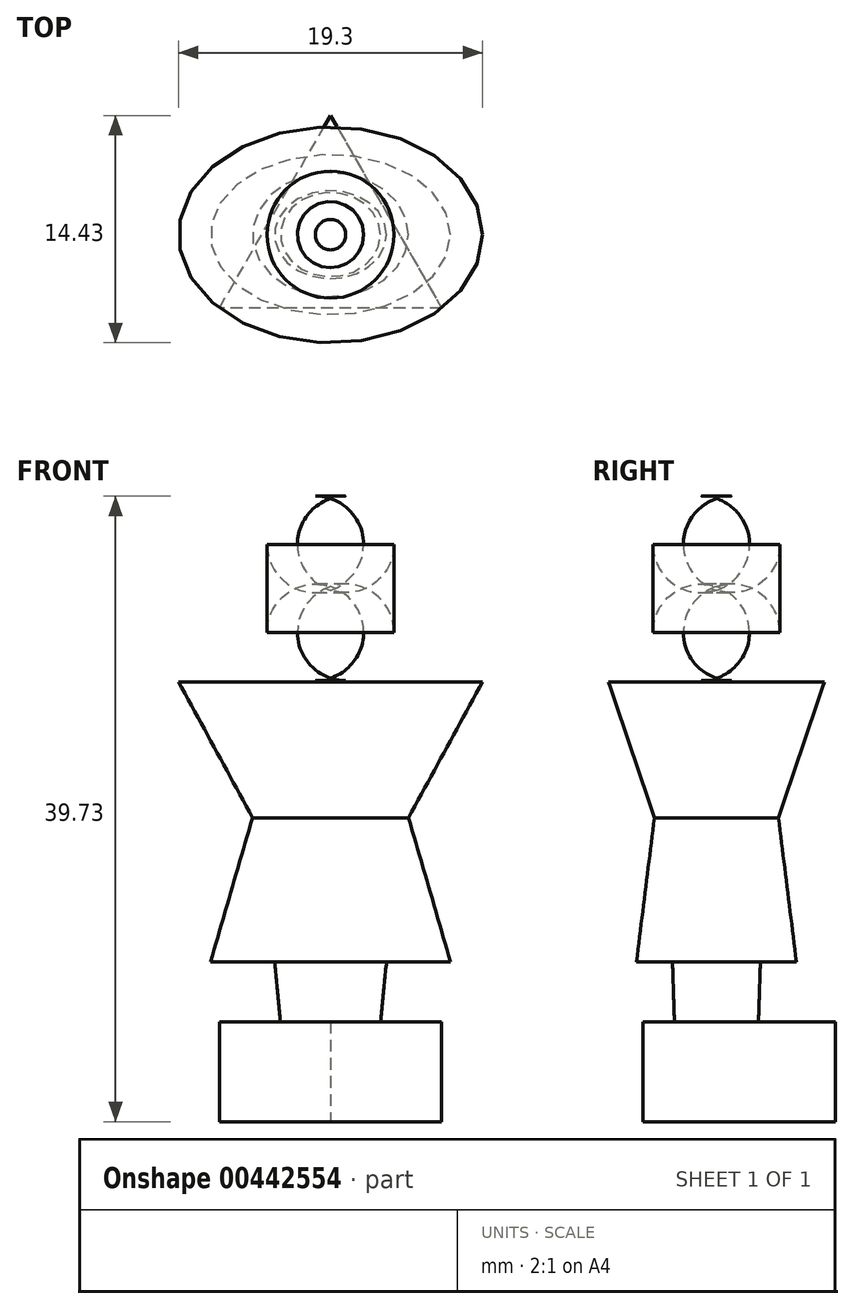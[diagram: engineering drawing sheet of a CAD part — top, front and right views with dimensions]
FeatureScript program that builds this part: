
annotation { "Feature Type Name" : "Feature", "Feature Type Description" : "" }
export const myFeature = defineFeature(function(context is Context, id is Id, definition is map)
    precondition{}
    {
        {
            var Q0;
            Q0=qCreatedBy(makeId("Top.planeOp"),FACE);
            var sketch = newSketch(context, id + "F0", { "sketchPlane" : qUnion([Q0])});
            skLineSegment(sketch, "E0", {"start": v(0, 7.57) * mm, "end": v(7.06, -4.66) * mm});
            skLineSegment(sketch, "E1", {"start": v(7.06, -4.66) * mm, "end": v(-7.06, -4.66) * mm});
            skLineSegment(sketch, "E2", {"start": v(-7.06, -4.66) * mm, "end": v(0, 7.57) * mm});
            skSolve(sketch);
        }
        {
            var Q0;
            Q0=makeQuery(id+"F0.imprint","IMPRINT",FACE,{"disambiguationData":[TD([[makeQuery(id+"F0.imprint","IMPRINT",EDGE,{"derivedFrom":sQuery(id+"F0.wireOp",EDGE,"E0")}),-1.0]])]});
            extrude(context, id + "F1", {"entities" : qUnion([Q0]), "depth" : 6.35 * mm});
        }
        {
            var Q0;
            Q0=makeQuery(id+"F1.opExtrude","CAP_FACE",FACE,{"disambiguationData":[OSD([sQuery(id+"F0.wireOp",EDGE,"E0"),sQuery(id+"F0.wireOp",EDGE,"E1"),sQuery(id+"F0.wireOp",EDGE,"E2"),sQuery(id+"F0.wireOp",EDGE,"QbnDVGJr-4Zaf-mHu2-ul8y-bYafnIeZrVXV")])],"isStart":false});
            var sketch = newSketch(context, id + "F2", { "sketchPlane" : qUnion([Q0])});
            skEllipse(sketch, "E3", {"center": v(0, 0) * mm, "majorRadius": 3.18 * mm, "minorRadius": 2.67 * mm, "majorAxis": v(1, 0)});
            skSolve(sketch);
        }
        {
            var Q0;
            Q0=makeQuery(id+"F2.imprint","IMPRINT",FACE,{"disambiguationData":[TD([[makeQuery(id+"F2.imprint","IMPRINT",EDGE,{"derivedFrom":sQuery(id+"F2.wireOp",EDGE,"E3")}),-1.0]])]});
            cPlane(context, id + "F3", {"entities" : qUnion([Q0]), "cplaneType" : CPlaneType.OFFSET, "offset" : 3.8 * mm, "width" : 152.4 * mm, "height" : 152.4 * mm});
        }
        {
            var Q0;
            Q0=qCreatedBy(id+"F3.planeOp",FACE);
            var sketch = newSketch(context, id + "F4", { "sketchPlane" : qUnion([Q0])});
            skEllipse(sketch, "E4", {"center": v(0, 0) * mm, "majorRadius": 3.56 * mm, "minorRadius": 2.8 * mm, "majorAxis": v(1, 0)});
            skSolve(sketch);
        }
        {
            var Q1;
            Q1=makeQuery(id+"F2.imprint","IMPRINT",FACE,{"disambiguationData":[TD([[makeQuery(id+"F2.imprint","IMPRINT",EDGE,{"derivedFrom":sQuery(id+"F2.wireOp",EDGE,"E3")}),1.0]])]});
            var Q2;
            Q2=makeQuery(id+"F4.imprint","IMPRINT",FACE,{"disambiguationData":[TD([[makeQuery(id+"F4.imprint","IMPRINT",EDGE,{"derivedFrom":sQuery(id+"F4.wireOp",EDGE,"E4")}),1.0]])]});
            loft(context, id + "F5", {"operationType" : NewBodyOperationType.ADD, "sheetProfilesArray" : [{ "sheetProfileEntities" : qUnion([Q1]) }, { "sheetProfileEntities" : qUnion([Q2]) }]});
        }
        {
            var Q0;
            Q0=qCreatedBy(id+"F3.planeOp",FACE);
            var sketch = newSketch(context, id + "F6", { "sketchPlane" : qUnion([Q0])});
            skEllipse(sketch, "E5", {"center": v(0, 0) * mm, "majorRadius": 7.62 * mm, "minorRadius": 5.08 * mm, "majorAxis": v(1, 0)});
            skSolve(sketch);
        }
        {
            var Q0;
            Q0=qCreatedBy(id+"F3.planeOp",FACE);
            cPlane(context, id + "F7", {"entities" : qUnion([Q0]), "cplaneType" : CPlaneType.OFFSET, "offset" : 9.14 * mm, "width" : 152.4 * mm, "height" : 152.4 * mm});
        }
        {
            var Q0;
            Q0=qCreatedBy(id+"F7.planeOp",FACE);
            var sketch = newSketch(context, id + "F8", { "sketchPlane" : qUnion([Q0])});
            skEllipse(sketch, "E6", {"center": v(0, 0) * mm, "majorRadius": 4.95 * mm, "minorRadius": 3.94 * mm, "majorAxis": v(1, 0)});
            skSolve(sketch);
        }
        {
            var Q1;
            Q1=makeQuery(id+"F8.imprint","IMPRINT",FACE,{"disambiguationData":[TD([[makeQuery(id+"F8.imprint","IMPRINT",EDGE,{"derivedFrom":sQuery(id+"F8.wireOp",EDGE,"E6")}),1.0]])]});
            var Q2;
            Q2=makeQuery(id+"F6.imprint","IMPRINT",FACE,{"disambiguationData":[TD([[makeQuery(id+"F6.imprint","IMPRINT",EDGE,{"derivedFrom":sQuery(id+"F6.wireOp",EDGE,"E5")}),1.0]])]});
            loft(context, id + "F9", {"operationType" : NewBodyOperationType.ADD, "sheetProfilesArray" : [{ "sheetProfileEntities" : qUnion([Q1]) }, { "sheetProfileEntities" : qUnion([Q2]) }]});
        }
        {
            var Q0;
            Q0=makeQuery(id+"F9.opLoft","CAP_FACE",FACE,{"disambiguationData":[OSD([makeQuery(id+"F8.imprint","IMPRINT",FACE,{"disambiguationData":[TD([[makeQuery(id+"F8.imprint","IMPRINT",EDGE,{"derivedFrom":sQuery(id+"F8.wireOp",EDGE,"E6")}),1.0]])]})])],"isStart":true});
            cPlane(context, id + "F10", {"entities" : qUnion([Q0]), "cplaneType" : CPlaneType.OFFSET, "offset" : 8.64 * mm, "width" : 152.4 * mm, "height" : 152.4 * mm});
        }
        {
            var Q0;
            Q0=qCreatedBy(id+"F10.planeOp",FACE);
            var sketch = newSketch(context, id + "F11", { "sketchPlane" : qUnion([Q0])});
            skEllipse(sketch, "E7", {"center": v(0, 0) * mm, "majorRadius": 9.65 * mm, "minorRadius": 6.86 * mm, "majorAxis": v(1, 0)});
            skSolve(sketch);
        }
        {
            var Q1;
            Q1=makeQuery(id+"F11.imprint","IMPRINT",FACE,{"disambiguationData":[TD([[makeQuery(id+"F11.imprint","IMPRINT",EDGE,{"derivedFrom":sQuery(id+"F11.wireOp",EDGE,"E7")}),1.0]])]});
            var Q2;
            Q2=makeQuery(id+"F9.opLoft","CAP_FACE",FACE,{"disambiguationData":[OSD([makeQuery(id+"F8.imprint","IMPRINT",FACE,{"disambiguationData":[TD([[makeQuery(id+"F8.imprint","IMPRINT",EDGE,{"derivedFrom":sQuery(id+"F8.wireOp",EDGE,"E6")}),1.0]])]})])],"isStart":true});
            loft(context, id + "F12", {"operationType" : NewBodyOperationType.ADD, "sheetProfilesArray" : [{ "sheetProfileEntities" : qUnion([Q1]) }, { "sheetProfileEntities" : qUnion([Q2]) }]});
        }
        {
            var Q0;
            Q0=qCreatedBy(makeId("Front.planeOp"),FACE);
            var sketch = newSketch(context, id + "F13", { "sketchPlane" : qUnion([Q0])});
            skLineSegment(sketch, "E8", {"start": v(0, 28.01) * mm, "end": v(0, 39.73) * mm});
            skLineSegment(sketch, "E9", {"start": v(0, 39.73) * mm, "end": v(4.03, 39.73) * mm});
            skLineSegment(sketch, "E10", {"start": v(4.03, 39.73) * mm, "end": v(4.03, 28.01) * mm});
            skLineSegment(sketch, "E11", {"start": v(4.03, 28.01) * mm, "end": v(0, 28.01) * mm});
            skSolve(sketch);
        }
        {
            var Q0;
            Q0=makeQuery(id+"F13.imprint","IMPRINT",FACE,{"disambiguationData":[TD([[makeQuery(id+"F13.imprint","IMPRINT",EDGE,{"derivedFrom":sQuery(id+"F13.wireOp",EDGE,"E8")}),-1.0]])]});
            var Q1;
            Q1=sQuery(id+"F13.wireOp",EDGE,"E8");
            revolve(context, id + "F14", {"entities" : qUnion([Q0]), "axis" : qUnion([Q1]), "revolveType" : RevolveType.FULL});
        }
        {
            var Q0;
            Q0=makeQuery(id+"F14.opRevolve","SWEPT_EDGE",EDGE,{"disambiguationData":[OSD([sQuery(id+"F13.wireOp",EDGE,"E9"),sQuery(id+"F13.wireOp",EDGE,"E10")])]});
            var Q1;
            Q1=makeQuery(id+"F14.opRevolve","SWEPT_EDGE",EDGE,{"disambiguationData":[OSD([sQuery(id+"F13.wireOp",EDGE,"E10"),sQuery(id+"F13.wireOp",EDGE,"E11")])]});
            fillet(context, id + "F15", {"entities" : qUnion([Q0, Q1]), "radius" : 3.07 * mm, "tangentPropagation" : true, "allowEdgeOverflow" : false});
        }
    });
